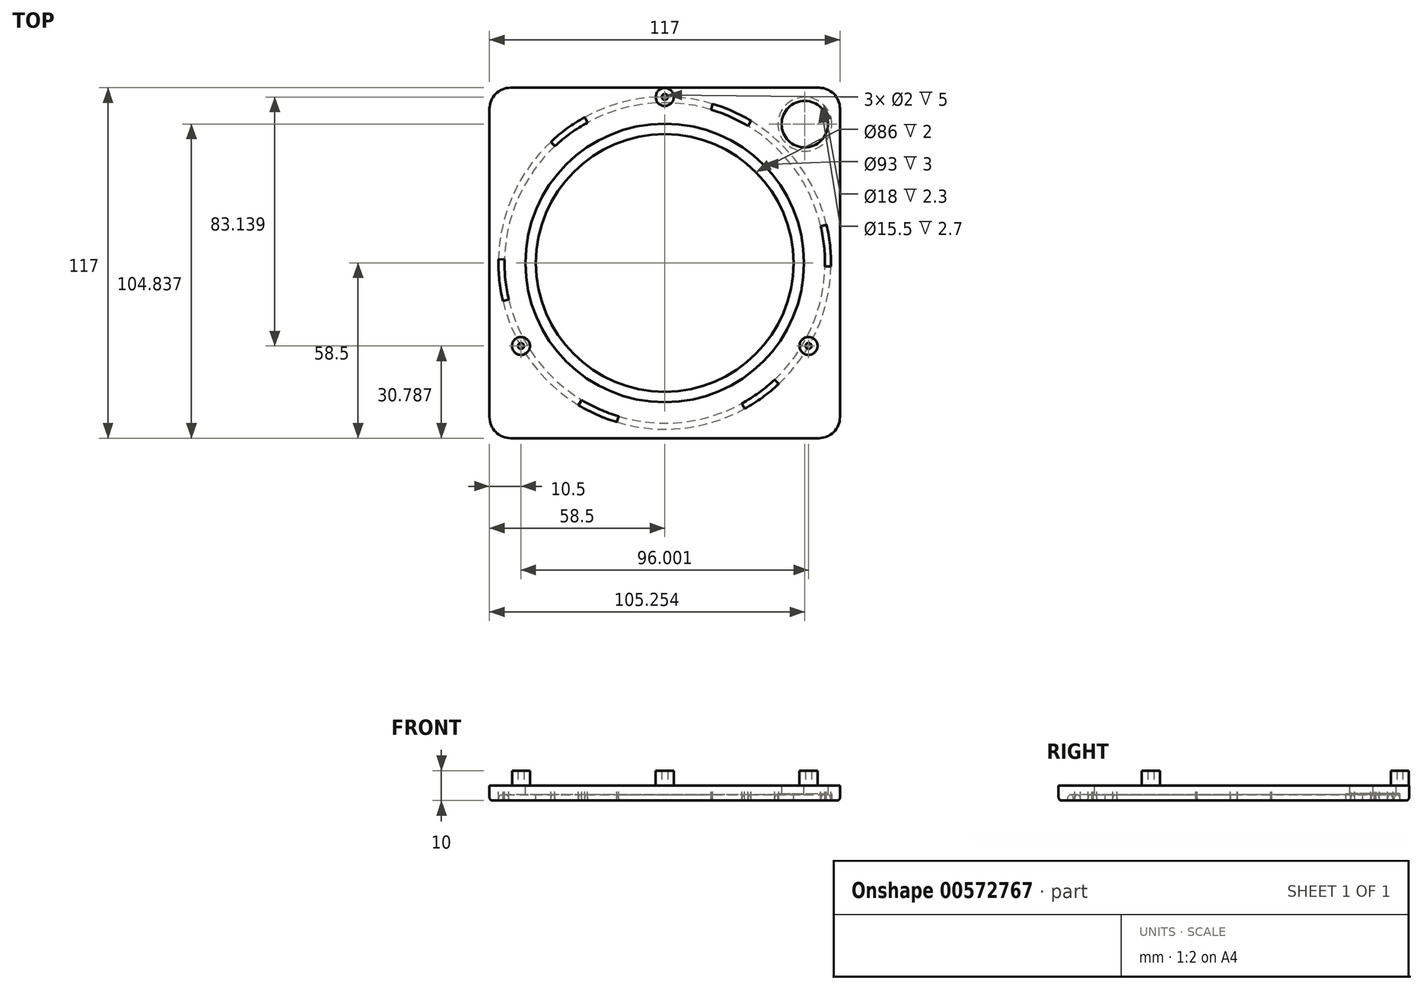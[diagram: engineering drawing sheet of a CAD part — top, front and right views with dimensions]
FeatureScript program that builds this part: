
annotation { "Feature Type Name" : "Feature", "Feature Type Description" : "" }
export const myFeature = defineFeature(function(context is Context, id is Id, definition is map)
    precondition{}
    {
        {
            var Q0;
            Q0=qCreatedBy(makeId("Top.planeOp"),FACE);
            var sketch = newSketch(context, id + "F0", { "sketchPlane" : qUnion([Q0])});
            skLineSegment(sketch, "E0.bottom", {"start": v(51.5, 58.5) * mm, "end": v(-51.5, 58.5) * mm});
            skLineSegment(sketch, "E0.top", {"start": v(51.5, -58.5) * mm, "end": v(-51.5, -58.5) * mm});
            skLineSegment(sketch, "E0.left", {"start": v(58.5, 51.5) * mm, "end": v(58.5, -51.5) * mm});
            skLineSegment(sketch, "E0.right", {"start": v(-58.5, 51.5) * mm, "end": v(-58.5, -51.5) * mm});
            skPoint(sketch, "E0.middle", {"position": v(0, 0) * mm});
            skPoint(sketch, "E1.visualSharp", {"position": v(-58.5, 58.5) * mm});
            skArc(sketch, "E1.filletArc", {"start": v(-51.5, 58.5) * mm, "mid": v(-56.45, 56.45) * mm, "end": v(-58.5, 51.5) * mm});
            skPoint(sketch, "E2.visualSharp", {"position": v(58.5, 58.5) * mm});
            skArc(sketch, "E2.filletArc", {"start": v(58.5, 51.5) * mm, "mid": v(56.45, 56.45) * mm, "end": v(51.5, 58.5) * mm});
            skPoint(sketch, "E3.visualSharp", {"position": v(58.5, -58.5) * mm});
            skArc(sketch, "E3.filletArc", {"start": v(51.5, -58.5) * mm, "mid": v(56.45, -56.45) * mm, "end": v(58.5, -51.5) * mm});
            skPoint(sketch, "E4.visualSharp", {"position": v(-58.5, -58.5) * mm});
            skArc(sketch, "E4.filletArc", {"start": v(-58.5, -51.5) * mm, "mid": v(-56.45, -56.45) * mm, "end": v(-51.5, -58.5) * mm});
            skSolve(sketch);
        }
        {
            var Q0;
            Q0 = qSketchRegion(id + "F0", true);
            extrude(context, id + "F1", {"entities" : qUnion([Q0]), "depth" : 5 * mm, "offsetDistance" : 25 * mm});
        }
        {
            var Q0;
            Q0=makeQuery(id+"F1.opExtrude","CAP_FACE",FACE,{"disambiguationData":[OSD([sQuery(id+"F0.wireOp",EDGE,"E0.bottom"),sQuery(id+"F0.wireOp",EDGE,"E0.top"),sQuery(id+"F0.wireOp",EDGE,"E0.left"),sQuery(id+"F0.wireOp",EDGE,"E0.right"),sQuery(id+"F0.wireOp",EDGE,"E1.filletArc"),sQuery(id+"F0.wireOp",EDGE,"E2.filletArc"),sQuery(id+"F0.wireOp",EDGE,"E3.filletArc"),sQuery(id+"F0.wireOp",EDGE,"E4.filletArc")])],"isStart":false});
            var sketch = newSketch(context, id + "F2", { "sketchPlane" : qUnion([Q0])});
            skCircle(sketch, "E5", {"center": v(0, 0) * mm, "radius": 43 * mm});
            skSolve(sketch);
        }
        {
            var Q0;
            Q0 = qSketchRegion(id + "F2", true);
            extrude(context, id + "F3", {"entities" : qUnion([Q0]), "operationType" : NewBodyOperationType.REMOVE, "endBound" : BoundingType.THROUGH_ALL, "oppositeDirection" : true, "depth" : 25 * mm, "offsetDistance" : 25 * mm});
        }
        {
            var Q0;
            Q0=makeQuery(id+"F1.opExtrude","CAP_FACE",FACE,{"disambiguationData":[OSD([sQuery(id+"F0.wireOp",EDGE,"E0.bottom"),sQuery(id+"F0.wireOp",EDGE,"E0.top"),sQuery(id+"F0.wireOp",EDGE,"E0.left"),sQuery(id+"F0.wireOp",EDGE,"E0.right"),sQuery(id+"F0.wireOp",EDGE,"E1.filletArc"),sQuery(id+"F0.wireOp",EDGE,"E2.filletArc"),sQuery(id+"F0.wireOp",EDGE,"E3.filletArc"),sQuery(id+"F0.wireOp",EDGE,"E4.filletArc")])],"isStart":false});
            var sketch = newSketch(context, id + "F4", { "sketchPlane" : qUnion([Q0])});
            skCircle(sketch, "E6", {"center": v(0, 0) * mm, "radius": 46.5 * mm});
            skSolve(sketch);
        }
        {
            var Q0;
            Q0 = qSketchRegion(id + "F4", true);
            extrude(context, id + "F5", {"entities" : qUnion([Q0]), "operationType" : NewBodyOperationType.REMOVE, "oppositeDirection" : true, "depth" : 3 * mm, "offsetDistance" : 25 * mm});
        }
        {
            var Q0;
            Q0=makeQuery(id+"F1.opExtrude","CAP_FACE",FACE,{"disambiguationData":[OSD([sQuery(id+"F0.wireOp",EDGE,"E0.bottom"),sQuery(id+"F0.wireOp",EDGE,"E0.top"),sQuery(id+"F0.wireOp",EDGE,"E0.left"),sQuery(id+"F0.wireOp",EDGE,"E0.right"),sQuery(id+"F0.wireOp",EDGE,"E1.filletArc"),sQuery(id+"F0.wireOp",EDGE,"E2.filletArc"),sQuery(id+"F0.wireOp",EDGE,"E3.filletArc"),sQuery(id+"F0.wireOp",EDGE,"E4.filletArc")])],"isStart":false});
            var sketch = newSketch(context, id + "F6", { "sketchPlane" : qUnion([Q0])});
            skSolve(sketch);
        }
        {
            var Q0;
            Q0=makeQuery(id+"F6.imprint","IMPRINT",FACE,{"disambiguationData":[TD([[makeQuery(id+"F6.imprint","IMPRINT",EDGE,{"derivedFrom":makeQuery(id+"F1.opExtrude","CAP_EDGE",EDGE,{"disambiguationData":[OSD([sQuery(id+"F0.wireOp",EDGE,"E0.bottom")])],"isStart":false})}),1.0]])]});
            var sketch = newSketch(context, id + "F7", { "sketchPlane" : qUnion([Q0])});
            skCircle(sketch, "E7", {"center": v(0, 55.43) * mm, "radius": 3 * mm});
            skPoint(sketch, "E8.center", {"position": v(0, 0) * mm});
            skCircle(sketch, "E9.0", {"center": v(0, 55.43) * mm, "radius": 1 * mm});
            skCircle(sketch, "E10", {"center": v(0, 0) * mm, "radius": 55.43 * mm, "construction": true});
            skCircle(sketch, "E11.1.0", {"center": v(-48, -27.71) * mm, "radius": 3 * mm});
            skCircle(sketch, "E11.1.1", {"center": v(-48, -27.71) * mm, "radius": 1 * mm});
            skCircle(sketch, "E11.2.0", {"center": v(48, -27.71) * mm, "radius": 3 * mm});
            skCircle(sketch, "E11.2.1", {"center": v(48, -27.71) * mm, "radius": 1 * mm});
            skLineSegment(sketch, "E12.bottom", {"start": v(57, 57) * mm, "end": v(-57, 57) * mm, "construction": true});
            skLineSegment(sketch, "E12.top", {"start": v(57, -57) * mm, "end": v(-57, -57) * mm, "construction": true});
            skLineSegment(sketch, "E12.left", {"start": v(57, 57) * mm, "end": v(57, -57) * mm, "construction": true});
            skLineSegment(sketch, "E12.right", {"start": v(-57, 57) * mm, "end": v(-57, -57) * mm, "construction": true});
            skSolve(sketch);
        }
        {
            var Q0;
            Q0 = qSketchRegion(id + "F7", true);
            extrude(context, id + "F8", {"entities" : qUnion([Q0]), "operationType" : NewBodyOperationType.ADD, "depth" : 5 * mm, "offsetDistance" : 25 * mm});
        }
        {
            var Q0;
            Q0=makeQuery(id+"F6.imprint","IMPRINT",FACE,{"disambiguationData":[TD([[makeQuery(id+"F6.imprint","IMPRINT",EDGE,{"derivedFrom":makeQuery(id+"F1.opExtrude","CAP_EDGE",EDGE,{"disambiguationData":[OSD([sQuery(id+"F0.wireOp",EDGE,"E0.bottom")])],"isStart":false})}),1.0]])]});
            var sketch = newSketch(context, id + "F9", { "sketchPlane" : qUnion([Q0])});
            skArc(sketch, "E13", {"start": v(28.79, 47.45) * mm, "mid": v(22.58, 50.7) * mm, "end": v(16, 53.14) * mm});
            skArc(sketch, "E14", {"start": v(27.75, 45.74) * mm, "mid": v(21.76, 48.87) * mm, "end": v(15.42, 51.23) * mm});
            skLineSegment(sketch, "E15", {"start": v(15.42, 51.23) * mm, "end": v(16, 53.14) * mm});
            skLineSegment(sketch, "E16", {"start": v(27.75, 45.74) * mm, "end": v(28.79, 47.45) * mm});
            skArc(sketch, "E17.1.0", {"start": v(-26.7, 48.66) * mm, "mid": v(-32.62, 44.9) * mm, "end": v(-38.02, 40.43) * mm});
            skLineSegment(sketch, "E17.1.1", {"start": v(-36.65, 38.97) * mm, "end": v(-38.02, 40.43) * mm});
            skArc(sketch, "E17.1.2", {"start": v(-25.74, 46.9) * mm, "mid": v(-31.45, 43.28) * mm, "end": v(-36.65, 38.97) * mm});
            skLineSegment(sketch, "E17.1.3", {"start": v(-25.74, 46.9) * mm, "end": v(-26.7, 48.66) * mm});
            skArc(sketch, "E17.2.0", {"start": v(-55.49, 1.2) * mm, "mid": v(-55.2, -5.8) * mm, "end": v(-54.02, -12.72) * mm});
            skLineSegment(sketch, "E17.2.1", {"start": v(-52.08, -12.26) * mm, "end": v(-54.02, -12.72) * mm});
            skArc(sketch, "E17.2.2", {"start": v(-53.49, 1.16) * mm, "mid": v(-53.2, -5.6) * mm, "end": v(-52.08, -12.26) * mm});
            skLineSegment(sketch, "E17.2.3", {"start": v(-53.49, 1.16) * mm, "end": v(-55.49, 1.2) * mm});
            skArc(sketch, "E17.3.0", {"start": v(-28.79, -47.45) * mm, "mid": v(-22.58, -50.7) * mm, "end": v(-16, -53.14) * mm});
            skLineSegment(sketch, "E17.3.1", {"start": v(-15.42, -51.23) * mm, "end": v(-16, -53.14) * mm});
            skArc(sketch, "E17.3.2", {"start": v(-27.75, -45.74) * mm, "mid": v(-21.76, -48.87) * mm, "end": v(-15.42, -51.23) * mm});
            skLineSegment(sketch, "E17.3.3", {"start": v(-27.75, -45.74) * mm, "end": v(-28.79, -47.45) * mm});
            skArc(sketch, "E17.4.0", {"start": v(26.7, -48.66) * mm, "mid": v(32.62, -44.9) * mm, "end": v(38.02, -40.43) * mm});
            skLineSegment(sketch, "E17.4.1", {"start": v(36.65, -38.97) * mm, "end": v(38.02, -40.43) * mm});
            skArc(sketch, "E17.4.2", {"start": v(25.74, -46.9) * mm, "mid": v(31.45, -43.28) * mm, "end": v(36.65, -38.97) * mm});
            skLineSegment(sketch, "E17.4.3", {"start": v(25.74, -46.9) * mm, "end": v(26.7, -48.66) * mm});
            skArc(sketch, "E17.5.0", {"start": v(55.49, -1.2) * mm, "mid": v(55.2, 5.8) * mm, "end": v(54.02, 12.72) * mm});
            skLineSegment(sketch, "E17.5.1", {"start": v(52.08, 12.26) * mm, "end": v(54.02, 12.72) * mm});
            skArc(sketch, "E17.5.2", {"start": v(53.49, -1.16) * mm, "mid": v(53.2, 5.6) * mm, "end": v(52.08, 12.26) * mm});
            skLineSegment(sketch, "E17.5.3", {"start": v(53.49, -1.16) * mm, "end": v(55.49, -1.2) * mm});
            skSolve(sketch);
        }
        {
            var Q0;
            Q0 = qSketchRegion(id + "F9", true);
            extrude(context, id + "F10", {"entities" : qUnion([Q0]), "operationType" : NewBodyOperationType.REMOVE, "endBound" : BoundingType.THROUGH_ALL, "oppositeDirection" : true, "depth" : 25 * mm, "offsetDistance" : 25 * mm});
        }
        {
            var Q0;
            Q0=makeQuery(id+"F1.opExtrude","CAP_FACE",FACE,{"disambiguationData":[OSD([sQuery(id+"F0.wireOp",EDGE,"E0.bottom"),sQuery(id+"F0.wireOp",EDGE,"E0.top"),sQuery(id+"F0.wireOp",EDGE,"E0.left"),sQuery(id+"F0.wireOp",EDGE,"E0.right"),sQuery(id+"F0.wireOp",EDGE,"E1.filletArc"),sQuery(id+"F0.wireOp",EDGE,"E2.filletArc"),sQuery(id+"F0.wireOp",EDGE,"E3.filletArc"),sQuery(id+"F0.wireOp",EDGE,"E4.filletArc")])],"isStart":true});
            var sketch = newSketch(context, id + "F11", { "sketchPlane" : qUnion([Q0])});
            skCircle(sketch, "E18", {"center": v(0, 0) * mm, "radius": 54.5 * mm});
            skSolve(sketch);
        }
        {
            var Q0;
            Q0=qCreatedBy(makeId("Right.planeOp"),FACE);
            var sketch = newSketch(context, id + "F12", { "sketchPlane" : qUnion([Q0])});
            skEllipse(sketch, "E19", {"center": v(-54.5, 0) * mm, "majorRadius": 1 * mm, "minorRadius": 2 * mm, "majorAxis": v(1, 0)});
            skSolve(sketch);
        }
        {
            var Q0;
            Q0=makeQuery(id+"F12.imprint","IMPRINT",FACE,{"disambiguationData":[TD([[makeQuery(id+"F12.imprint","IMPRINT",EDGE,{"derivedFrom":sQuery(id+"F12.wireOp",EDGE,"E19")}),1.0]])]});
            var Q1;
            Q1=sQuery(id+"F11.wireOp",EDGE,"E18");
            sweep(context, id + "F13", {"operationType" : NewBodyOperationType.REMOVE, "profiles" : qUnion([Q0]), "path" : qUnion([Q1])});
        }
        {
            var Q0;
            Q0=makeQuery(id+"F1.opExtrude","CAP_EDGE",EDGE,{"disambiguationData":[OSD([sQuery(id+"F0.wireOp",EDGE,"E0.right")])],"isStart":true});
            var Q1;
            Q1=makeQuery(id+"F1.opExtrude","CAP_EDGE",EDGE,{"disambiguationData":[OSD([sQuery(id+"F0.wireOp",EDGE,"E1.filletArc")])],"isStart":true});
            var Q2;
            Q2=makeQuery(id+"F1.opExtrude","CAP_EDGE",EDGE,{"disambiguationData":[OSD([sQuery(id+"F0.wireOp",EDGE,"E0.bottom")])],"isStart":true});
            var Q3;
            Q3=makeQuery(id+"F1.opExtrude","CAP_EDGE",EDGE,{"disambiguationData":[OSD([sQuery(id+"F0.wireOp",EDGE,"E0.top")])],"isStart":true});
            var Q4;
            Q4=makeQuery(id+"F1.opExtrude","CAP_EDGE",EDGE,{"disambiguationData":[OSD([sQuery(id+"F0.wireOp",EDGE,"E4.filletArc")])],"isStart":true});
            var Q5;
            Q5=makeQuery(id+"F1.opExtrude","CAP_EDGE",EDGE,{"disambiguationData":[OSD([sQuery(id+"F0.wireOp",EDGE,"E2.filletArc")])],"isStart":true});
            var Q6;
            Q6=makeQuery(id+"F1.opExtrude","CAP_EDGE",EDGE,{"disambiguationData":[OSD([sQuery(id+"F0.wireOp",EDGE,"E0.left")])],"isStart":true});
            var Q7;
            Q7=makeQuery(id+"F1.opExtrude","CAP_EDGE",EDGE,{"disambiguationData":[OSD([sQuery(id+"F0.wireOp",EDGE,"E3.filletArc")])],"isStart":true});
            fillet(context, id + "F14", {"entities" : qUnion([Q0, Q1, Q2, Q3, Q4, Q5, Q6, Q7]), "radius" : 1 * mm, "tangentPropagation" : true, "allowEdgeOverflow" : false});
        }
        {
            var Q0;
            {var subQ0=sQuery(id+"F0.wireOp",EDGE,"E0.left");var subQ1=sQuery(id+"F0.wireOp",EDGE,"E0.right");var subQ2=sQuery(id+"F0.wireOp",EDGE,"E0.bottom");var subQ3=sQuery(id+"F0.wireOp",EDGE,"E1.filletArc");var subQ4=sQuery(id+"F0.wireOp",EDGE,"E2.filletArc");var subQ5=sQuery(id+"F0.wireOp",EDGE,"E3.filletArc");var subQ6=sQuery(id+"F0.wireOp",EDGE,"E0.top");var subQ7=sQuery(id+"F0.wireOp",EDGE,"E4.filletArc");Q0=makeQuery(id+"F13.boolean.opBoolean","SPLIT",FACE,{"disambiguationData":[TD([makeQuery(id+"F1.opExtrude","SWEPT_FACE",FACE,{"disambiguationData":[OSD([subQ2])]})])],"derivedFrom":makeQuery(id+"F1.opExtrude","CAP_FACE",FACE,{"disambiguationData":[OSD([subQ2,subQ6,subQ0,subQ1,subQ3,subQ4,subQ5,subQ7])],"isStart":true})});}
            var sketch = newSketch(context, id + "F15", { "sketchPlane" : qUnion([Q0])});
            skCircle(sketch, "E20", {"center": v(46.75, -46.34) * mm, "radius": 9 * mm});
            skSolve(sketch);
        }
        {
            var Q0;
            Q0 = qSketchRegion(id + "F15", true);
            extrude(context, id + "F16", {"entities" : qUnion([Q0]), "operationType" : NewBodyOperationType.REMOVE, "oppositeDirection" : true, "depth" : 2.3 * mm, "offsetDistance" : 25 * mm});
        }
        {
            var Q0;
            Q0=makeQuery(id+"F16.boolean.opBoolean","COPY",FACE,{"derivedFrom":makeQuery(id+"F16.opExtrude","CAP_FACE",FACE,{"disambiguationData":[OSD([sQuery(id+"F15.wireOp",EDGE,"E20")])],"isStart":false})});
            var sketch = newSketch(context, id + "F17", { "sketchPlane" : qUnion([Q0])});
            skCircle(sketch, "E21", {"center": v(46.75, -46.34) * mm, "radius": 7.75 * mm});
            skSolve(sketch);
        }
        {
            var Q0;
            Q0 = qSketchRegion(id + "F17", true);
            extrude(context, id + "F18", {"entities" : qUnion([Q0]), "operationType" : NewBodyOperationType.REMOVE, "endBound" : BoundingType.THROUGH_ALL, "oppositeDirection" : true, "depth" : 25 * mm, "offsetDistance" : 25 * mm});
        }
    });
